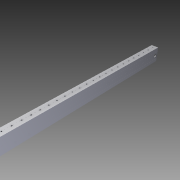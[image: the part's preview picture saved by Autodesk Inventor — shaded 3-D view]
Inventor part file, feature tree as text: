
AUTODESK INVENTOR PART (.ipt)
format: ipt  version: 2014 SP1 (Build 180222100, 222)  size: 738,304 bytes
history: native  units: in
note: dims shown in document units (in); Inventor stores cm internally (conversion verified against a paired STEP export)
features: other x2, extrude x2, sketch x2, imported_body x1
ambient origin geometry x8: Origin, YZ Plane, XZ Plane, XY Plane, X Axis, Y Axis, Z Axis, Center Point
bodies: Body1 (feature_tree)
feature tree (7):
  other  "Cut-Extrude2"
  other  "2x1 Tube1"
  extrude  "Extrusion1"  Depth=0.5in
  extrude  "Extrusion2"  Depth=1.0in TaperAngle=0.0deg
  imported_body  "Base1"
  sketch  "Sketch1"  dims[d0=35.0in d1=0.0in d2=0.5in]
  sketch  "Sketch2"  dims[d3=0.5in d4=1.0in d5=0.0in]
